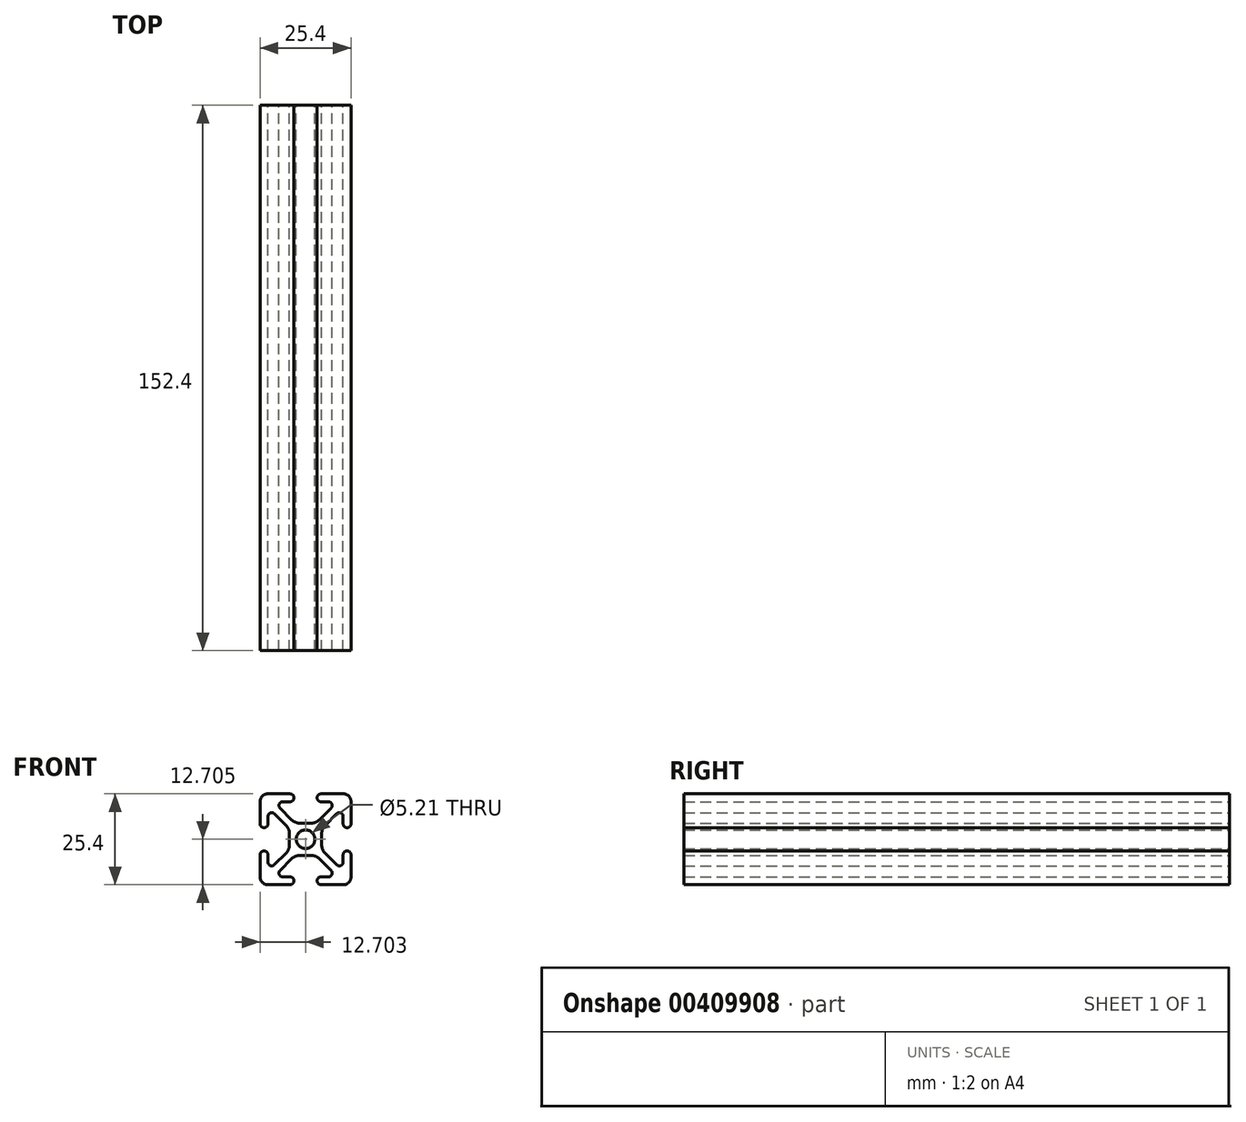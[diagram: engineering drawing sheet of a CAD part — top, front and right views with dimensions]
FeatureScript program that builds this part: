
annotation { "Feature Type Name" : "Feature", "Feature Type Description" : "" }
export const myFeature = defineFeature(function(context is Context, id is Id, definition is map)
    precondition{}
    {
        {
            var Q0;
            Q0=qCreatedBy(makeId("Front.planeOp"),FACE);
            var sketch = newSketch(context, id + "F0", { "sketchPlane" : qUnion([Q0])});
            skArc(sketch, "E0", {"start": v(-10.62, 12.76) * mm, "mid": v(-12.1, 12.15) * mm, "end": v(-12.73, 10.66) * mm});
            skArc(sketch, "E1", {"start": v(-12.73, 4.4) * mm, "mid": v(-11.62, 3.3) * mm, "end": v(-10.52, 4.4) * mm});
            skArc(sketch, "E2", {"start": v(-4.37, 10.55) * mm, "mid": v(-3.27, 11.66) * mm, "end": v(-4.37, 12.76) * mm});
            skArc(sketch, "E3", {"start": v(-8.75, 7.2) * mm, "mid": v(-9.88, 7.42) * mm, "end": v(-10.52, 6.46) * mm});
            skArc(sketch, "E4", {"start": v(-6.43, 10.55) * mm, "mid": v(-7.38, 9.92) * mm, "end": v(-7.16, 8.8) * mm});
            skLineSegment(sketch, "E5", {"start": v(-12.73, 10.66) * mm, "end": v(-12.73, 4.4) * mm});
            skLineSegment(sketch, "E6", {"start": v(-10.62, 12.76) * mm, "end": v(-4.37, 12.76) * mm});
            skLineSegment(sketch, "E7", {"start": v(-10.52, 4.4) * mm, "end": v(-10.52, 6.46) * mm});
            skLineSegment(sketch, "E8", {"start": v(-4.37, 10.55) * mm, "end": v(-6.43, 10.55) * mm});
            skLineSegment(sketch, "E9", {"start": v(-11.51, 7.5) * mm, "end": v(-10.3, 7.5) * mm, "construction": true});
            skLineSegment(sketch, "E10", {"start": v(-13.64, 3.3) * mm, "end": v(-12.36, 3.3) * mm, "construction": true});
            skLineSegment(sketch, "E11", {"start": v(-7.46, 11.03) * mm, "end": v(-7.46, 8.91) * mm, "construction": true});
            skLineSegment(sketch, "E12", {"start": v(-3.27, 12.37) * mm, "end": v(-3.27, 10.25) * mm, "construction": true});
            skLineSegment(sketch, "E13.bottom", {"start": v(1.57, 4.57) * mm, "end": v(-1.63, 4.57) * mm});
            skLineSegment(sketch, "E13.top", {"start": v(1.57, -4.44) * mm, "end": v(-1.63, -4.44) * mm});
            skLineSegment(sketch, "E13.left", {"start": v(4.48, 1.66) * mm, "end": v(4.48, -1.53) * mm});
            skLineSegment(sketch, "E13.right", {"start": v(-4.54, 1.66) * mm, "end": v(-4.54, -1.53) * mm});
            skPoint(sketch, "E13.middle", {"position": v(-0.03, 0.06) * mm});
            skLineSegment(sketch, "E14", {"start": v(-8.75, 7.2) * mm, "end": v(-5.47, 3.9) * mm});
            skLineSegment(sketch, "E15", {"start": v(-7.16, 8.8) * mm, "end": v(-3.87, 5.5) * mm});
            skArc(sketch, "E16.filletArc", {"start": v(-3.87, 5.5) * mm, "mid": v(-2.84, 4.81) * mm, "end": v(-1.63, 4.57) * mm});
            skArc(sketch, "E17.filletArc", {"start": v(-4.54, 1.66) * mm, "mid": v(-4.78, 2.88) * mm, "end": v(-5.47, 3.9) * mm});
            skLineSegment(sketch, "E18", {"start": v(5.32, 0.06) * mm, "end": v(-7.21, 0.06) * mm, "construction": true});
            skPoint(sketch, "E18.startSnap0", {"position": v(2.97, 0.06) * mm});
            skPoint(sketch, "E19", {"position": v(-0.03, -4.44) * mm});
            skLineSegment(sketch, "E20", {"start": v(-0.03, -6.76) * mm, "end": v(-0.03, 5.83) * mm, "construction": true});
            skLineSegment(sketch, "E21.MirrorCS", {"start": v(11.46, 7.5) * mm, "end": v(10.25, 7.5) * mm, "construction": true});
            skArc(sketch, "E22.MirrorCS", {"start": v(10.57, 12.76) * mm, "mid": v(12.06, 12.15) * mm, "end": v(12.67, 10.66) * mm});
            skLineSegment(sketch, "E23.MirrorCS", {"start": v(7.4, 11.03) * mm, "end": v(7.4, 8.91) * mm, "construction": true});
            skLineSegment(sketch, "E24.MirrorCS", {"start": v(10.46, 4.4) * mm, "end": v(10.46, 6.46) * mm});
            skArc(sketch, "E25.MirrorCS", {"start": v(3.82, 5.5) * mm, "mid": v(2.79, 4.81) * mm, "end": v(1.57, 4.57) * mm});
            skLineSegment(sketch, "E26.MirrorCS", {"start": v(8.7, 7.2) * mm, "end": v(5.41, 3.9) * mm});
            skLineSegment(sketch, "E27.MirrorCS", {"start": v(3.21, 12.37) * mm, "end": v(3.21, 10.25) * mm, "construction": true});
            skLineSegment(sketch, "E28.MirrorCS", {"start": v(13.58, 3.3) * mm, "end": v(12.3, 3.3) * mm, "construction": true});
            skArc(sketch, "E29.MirrorCS", {"start": v(4.32, 10.55) * mm, "mid": v(3.21, 11.66) * mm, "end": v(4.32, 12.76) * mm});
            skArc(sketch, "E30.MirrorCS", {"start": v(8.7, 7.2) * mm, "mid": v(9.83, 7.42) * mm, "end": v(10.46, 6.46) * mm});
            skArc(sketch, "E31.MirrorCS", {"start": v(12.67, 4.4) * mm, "mid": v(11.57, 3.3) * mm, "end": v(10.46, 4.4) * mm});
            skLineSegment(sketch, "E32.MirrorCS", {"start": v(10.57, 12.76) * mm, "end": v(4.32, 12.76) * mm});
            skLineSegment(sketch, "E33.MirrorCS", {"start": v(12.67, 10.66) * mm, "end": v(12.67, 4.4) * mm});
            skArc(sketch, "E34.MirrorCS", {"start": v(6.37, 10.55) * mm, "mid": v(7.33, 9.92) * mm, "end": v(7.1, 8.8) * mm});
            skLineSegment(sketch, "E35.MirrorCS", {"start": v(7.1, 8.8) * mm, "end": v(3.82, 5.5) * mm});
            skLineSegment(sketch, "E36.MirrorCS", {"start": v(4.32, 10.55) * mm, "end": v(6.37, 10.55) * mm});
            skArc(sketch, "E37.MirrorCS", {"start": v(4.48, 1.66) * mm, "mid": v(4.72, 2.88) * mm, "end": v(5.41, 3.9) * mm});
            skLineSegment(sketch, "E38.MirrorCS", {"start": v(-11.51, -7.37) * mm, "end": v(-10.3, -7.37) * mm, "construction": true});
            skArc(sketch, "E39.MirrorCS", {"start": v(-3.87, -5.37) * mm, "mid": v(-2.84, -4.69) * mm, "end": v(-1.63, -4.44) * mm});
            skArc(sketch, "E40.MirrorCS", {"start": v(-10.62, -12.64) * mm, "mid": v(-12.1, -12.02) * mm, "end": v(-12.73, -10.53) * mm});
            skArc(sketch, "E41.MirrorCS", {"start": v(-8.75, -7.07) * mm, "mid": v(-9.88, -7.3) * mm, "end": v(-10.52, -6.33) * mm});
            skArc(sketch, "E42.MirrorCS", {"start": v(-6.43, -10.43) * mm, "mid": v(-7.38, -9.79) * mm, "end": v(-7.16, -8.66) * mm});
            skLineSegment(sketch, "E43.MirrorCS", {"start": v(-3.27, -12.24) * mm, "end": v(-3.27, -10.12) * mm, "construction": true});
            skArc(sketch, "E44.MirrorCS", {"start": v(-4.54, -1.53) * mm, "mid": v(-4.78, -2.75) * mm, "end": v(-5.47, -3.78) * mm});
            skLineSegment(sketch, "E45.MirrorCS", {"start": v(-12.73, -10.53) * mm, "end": v(-12.73, -4.28) * mm});
            skLineSegment(sketch, "E46.MirrorCS", {"start": v(-13.64, -3.17) * mm, "end": v(-12.36, -3.17) * mm, "construction": true});
            skLineSegment(sketch, "E47.MirrorCS", {"start": v(-7.46, -10.9) * mm, "end": v(-7.46, -8.78) * mm, "construction": true});
            skLineSegment(sketch, "E48.MirrorCS", {"start": v(-4.37, -10.43) * mm, "end": v(-6.43, -10.43) * mm});
            skLineSegment(sketch, "E49.MirrorCS", {"start": v(-10.62, -12.64) * mm, "end": v(-4.37, -12.64) * mm});
            skLineSegment(sketch, "E50.MirrorCS", {"start": v(-10.52, -4.28) * mm, "end": v(-10.52, -6.33) * mm});
            skArc(sketch, "E51.MirrorCS", {"start": v(-12.73, -4.28) * mm, "mid": v(-11.62, -3.17) * mm, "end": v(-10.52, -4.28) * mm});
            skLineSegment(sketch, "E52.MirrorCS", {"start": v(-8.75, -7.07) * mm, "end": v(-5.47, -3.78) * mm});
            skLineSegment(sketch, "E53.MirrorCS", {"start": v(-7.16, -8.66) * mm, "end": v(-3.87, -5.37) * mm});
            skArc(sketch, "E54.MirrorCS", {"start": v(-4.37, -10.43) * mm, "mid": v(-3.27, -11.53) * mm, "end": v(-4.37, -12.64) * mm});
            skLineSegment(sketch, "E55.MirrorCS", {"start": v(11.46, -7.37) * mm, "end": v(10.25, -7.37) * mm, "construction": true});
            skArc(sketch, "E56.MirrorCS", {"start": v(4.32, -10.43) * mm, "mid": v(3.21, -11.53) * mm, "end": v(4.32, -12.64) * mm});
            skLineSegment(sketch, "E57.MirrorCS", {"start": v(13.58, -3.17) * mm, "end": v(12.3, -3.17) * mm, "construction": true});
            skArc(sketch, "E58.MirrorCS", {"start": v(8.7, -7.07) * mm, "mid": v(9.83, -7.3) * mm, "end": v(10.46, -6.33) * mm});
            skLineSegment(sketch, "E59.MirrorCS", {"start": v(7.1, -8.66) * mm, "end": v(3.82, -5.37) * mm});
            skLineSegment(sketch, "E60.MirrorCS", {"start": v(7.4, -10.9) * mm, "end": v(7.4, -8.78) * mm, "construction": true});
            skLineSegment(sketch, "E61.MirrorCS", {"start": v(3.21, -12.24) * mm, "end": v(3.21, -10.12) * mm, "construction": true});
            skLineSegment(sketch, "E62.MirrorCS", {"start": v(4.32, -10.43) * mm, "end": v(6.37, -10.43) * mm});
            skArc(sketch, "E63.MirrorCS", {"start": v(3.82, -5.37) * mm, "mid": v(2.79, -4.69) * mm, "end": v(1.57, -4.44) * mm});
            skArc(sketch, "E64.MirrorCS", {"start": v(10.57, -12.64) * mm, "mid": v(12.06, -12.02) * mm, "end": v(12.67, -10.53) * mm});
            skLineSegment(sketch, "E65.MirrorCS", {"start": v(10.57, -12.64) * mm, "end": v(4.32, -12.64) * mm});
            skLineSegment(sketch, "E66.MirrorCS", {"start": v(8.7, -7.07) * mm, "end": v(5.41, -3.78) * mm});
            skLineSegment(sketch, "E67.MirrorCS", {"start": v(12.67, -10.53) * mm, "end": v(12.67, -4.28) * mm});
            skArc(sketch, "E68.MirrorCS", {"start": v(12.67, -4.28) * mm, "mid": v(11.57, -3.17) * mm, "end": v(10.46, -4.28) * mm});
            skArc(sketch, "E69.MirrorCS", {"start": v(4.48, -1.53) * mm, "mid": v(4.72, -2.75) * mm, "end": v(5.41, -3.78) * mm});
            skLineSegment(sketch, "E70.MirrorCS", {"start": v(10.46, -4.28) * mm, "end": v(10.46, -6.33) * mm});
            skArc(sketch, "E71.MirrorCS", {"start": v(6.37, -10.43) * mm, "mid": v(7.33, -9.79) * mm, "end": v(7.1, -8.66) * mm});
            skCircle(sketch, "E72", {"center": v(-0.03, 0.06) * mm, "radius": 2.6 * mm});
            skSolve(sketch);
        }
        {
            var Q0;
            Q0=qSketchRegion(id+"F0",true);
            extrude(context, id + "F1", {"entities" : qUnion([Q0]), "depth" : 152.4 * mm});
        }
    });
